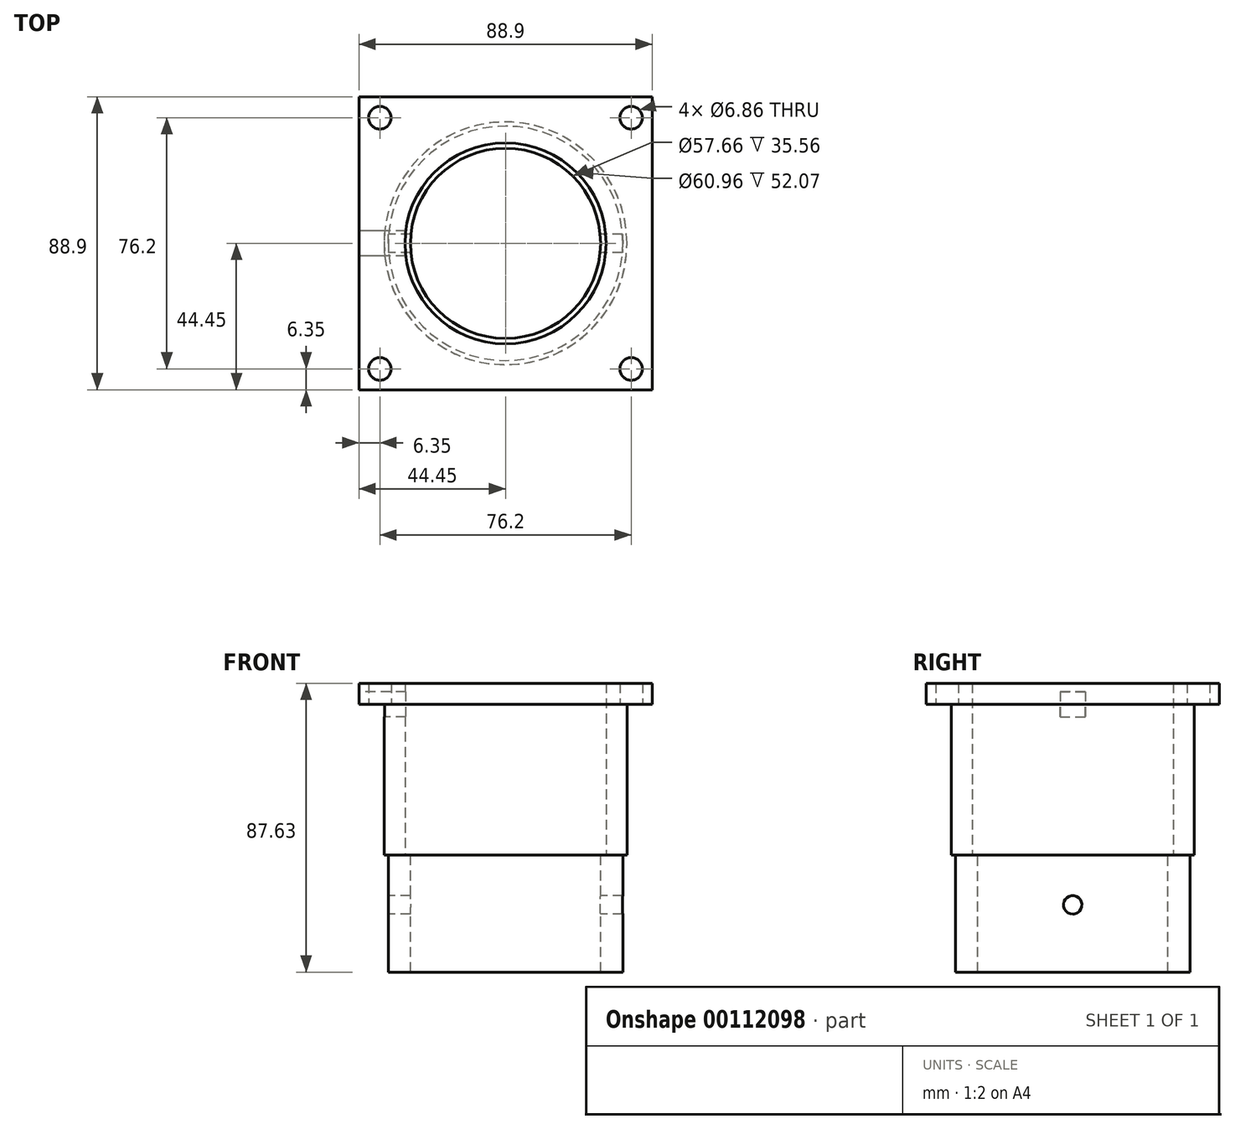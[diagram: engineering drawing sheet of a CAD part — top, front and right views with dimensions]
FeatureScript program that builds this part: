
annotation { "Feature Type Name" : "Feature", "Feature Type Description" : "" }
export const myFeature = defineFeature(function(context is Context, id is Id, definition is map)
    precondition{}
    {
        {
            var Q0;
            Q0=qCreatedBy(makeId("Top.planeOp"),FACE);
            var sketch = newSketch(context, id + "F0", { "sketchPlane" : qUnion([Q0])});
            skLineSegment(sketch, "E0.bottom", {"start": v(44.45, -44.45) * mm, "end": v(-44.45, -44.45) * mm});
            skLineSegment(sketch, "E0.top", {"start": v(44.45, 44.45) * mm, "end": v(-44.45, 44.45) * mm});
            skLineSegment(sketch, "E0.left", {"start": v(44.45, -44.45) * mm, "end": v(44.45, 44.45) * mm});
            skLineSegment(sketch, "E0.right", {"start": v(-44.45, -44.45) * mm, "end": v(-44.45, 44.45) * mm});
            skPoint(sketch, "E0.middle", {"position": v(0, 0) * mm});
            skCircle(sketch, "E1", {"center": v(-38.1, -38.1) * mm, "radius": 3.43 * mm});
            skCircle(sketch, "E2", {"center": v(-38.1, 38.1) * mm, "radius": 3.43 * mm});
            skCircle(sketch, "E3", {"center": v(38.1, -38.1) * mm, "radius": 3.43 * mm});
            skCircle(sketch, "E4", {"center": v(38.1, 38.1) * mm, "radius": 3.43 * mm});
            skSolve(sketch);
        }
        {
            var Q0;
            Q0 = qSketchRegion(id + "F0", true);
            extrude(context, id + "F1", {"entities" : qUnion([Q0]), "depth" : 6.35 * mm});
        }
        {
            var Q0;
            Q0=makeQuery(id+"F1.opExtrude","CAP_FACE",FACE,{"disambiguationData":[OSD([sQuery(id+"F0.wireOp",EDGE,"E0.bottom"),sQuery(id+"F0.wireOp",EDGE,"E0.top"),sQuery(id+"F0.wireOp",EDGE,"E0.left"),sQuery(id+"F0.wireOp",EDGE,"E0.right"),sQuery(id+"F0.wireOp",EDGE,"E1"),sQuery(id+"F0.wireOp",EDGE,"E2"),sQuery(id+"F0.wireOp",EDGE,"E3"),sQuery(id+"F0.wireOp",EDGE,"E4")])],"isStart":true});
            var sketch = newSketch(context, id + "F2", { "sketchPlane" : qUnion([Q0])});
            skCircle(sketch, "E5", {"center": v(0, 0) * mm, "radius": 30.48 * mm});
            skSolve(sketch);
        }
        {
            var Q0;
            Q0=makeQuery(id+"F2.imprint","IMPRINT",FACE,{"disambiguationData":[TD([[makeQuery(id+"F2.imprint","IMPRINT",EDGE,{"derivedFrom":sQuery(id+"F2.wireOp",EDGE,"E5")}),1.0]])]});
            var Q1;
            Q1=sQuery(id+"F2.wireOp",EDGE,"E5");
            extrude(context, id + "F3", {"entities" : qUnion([Q0]), "operationType" : NewBodyOperationType.REMOVE, "surfaceEntities" : qUnion([Q1]), "endBound" : BoundingType.THROUGH_ALL, "oppositeDirection" : true, "depth" : 25.4 * mm});
        }
        {
            var Q0;
            Q0=qCreatedBy(makeId("Top.planeOp"),FACE);
            var sketch = newSketch(context, id + "F4", { "sketchPlane" : qUnion([Q0])});
            skCircle(sketch, "E6", {"center": v(0, 0) * mm, "radius": 36.83 * mm});
            skCircle(sketch, "E7", {"center": v(0, 0) * mm, "radius": 30.48 * mm});
            skSolve(sketch);
        }
        {
            var Q0;
            Q0=makeQuery(id+"F4.imprint","IMPRINT",FACE,{"disambiguationData":[TD([[makeQuery(id+"F4.imprint","IMPRINT",EDGE,{"derivedFrom":sQuery(id+"F4.wireOp",EDGE,"E6")}),1.0]])]});
            extrude(context, id + "F5", {"entities" : qUnion([Q0]), "operationType" : NewBodyOperationType.ADD, "oppositeDirection" : true, "depth" : 45.72 * mm});
        }
        {
            var Q0;
            Q0=makeQuery(id+"F5.opExtrude","CAP_FACE",FACE,{"disambiguationData":[OSD([sQuery(id+"F4.wireOp",EDGE,"E6"),sQuery(id+"F4.wireOp",EDGE,"E7")])],"isStart":false});
            var sketch = newSketch(context, id + "F6", { "sketchPlane" : qUnion([Q0])});
            skCircle(sketch, "E8", {"center": v(0, 0) * mm, "radius": 28.83 * mm});
            skCircle(sketch, "E9", {"center": v(0, 0) * mm, "radius": 35.56 * mm});
            skSolve(sketch);
        }
        {
            var Q0;
            Q0 = qSketchRegion(id + "F6", true);
            extrude(context, id + "F7", {"entities" : qUnion([Q0]), "operationType" : NewBodyOperationType.ADD, "depth" : 35.56 * mm});
        }
        {
            var Q0;
            Q0=makeQuery(id+"F1.opExtrude","SWEPT_FACE",FACE,{"disambiguationData":[OSD([sQuery(id+"F0.wireOp",EDGE,"E0.right")])]});
            var sketch = newSketch(context, id + "F8", { "sketchPlane" : qUnion([Q0])});
            skSolve(sketch);
        }
        {
            var Q0;
            {var subQ0=sQuery(id+"F0.wireOp",EDGE,"E0.right");Q0=makeQuery(id+"F8.imprint","IMPRINT",FACE,{"disambiguationData":[TD([[makeQuery(id+"F8.imprint","IMPRINT",EDGE,{"derivedFrom":makeQuery(id+"F1.opExtrude","CAP_EDGE",EDGE,{"disambiguationData":[OSD([subQ0])],"isStart":true})}),-1.0]])]});}
            var sketch = newSketch(context, id + "F9", { "sketchPlane" : qUnion([Q0])});
            skLineSegment(sketch, "E10.bottom", {"start": v(-3.81, 3.81) * mm, "end": v(3.81, 3.81) * mm});
            skLineSegment(sketch, "E10.top", {"start": v(-3.81, -3.81) * mm, "end": v(3.81, -3.81) * mm});
            skLineSegment(sketch, "E10.left", {"start": v(-3.81, 3.81) * mm, "end": v(-3.81, -3.81) * mm});
            skLineSegment(sketch, "E10.right", {"start": v(3.81, 3.81) * mm, "end": v(3.81, -3.81) * mm});
            skPoint(sketch, "E10.middle", {"position": v(0, 0) * mm});
            skSolve(sketch);
        }
        {
            var Q0;
            Q0 = qSketchRegion(id + "F9", true);
            extrude(context, id + "F10", {"entities" : qUnion([Q0]), "operationType" : NewBodyOperationType.REMOVE, "oppositeDirection" : true, "depth" : 25.5 * mm});
        }
        {
            var Q0;
            Q0=qCreatedBy(makeId("Right.planeOp"),FACE);
            var sketch = newSketch(context, id + "F11", { "sketchPlane" : qUnion([Q0])});
            skCircle(sketch, "E11", {"center": v(0, -60.86) * mm, "radius": 2.8 * mm});
            skSolve(sketch);
        }
        {
            var Q0;
            Q0=makeQuery(id+"F11.imprint","IMPRINT",FACE,{"disambiguationData":[TD([[makeQuery(id+"F11.imprint","IMPRINT",EDGE,{"derivedFrom":sQuery(id+"F11.wireOp",EDGE,"E11")}),1.0]])]});
            var Q1;
            Q1=sQuery(id+"F11.wireOp",EDGE,"E11");
            extrude(context, id + "F12", {"entities" : qUnion([Q0]), "operationType" : NewBodyOperationType.REMOVE, "surfaceEntities" : qUnion([Q1]), "depth" : 88.9 * mm, "symmetric" : true});
        }
    });
